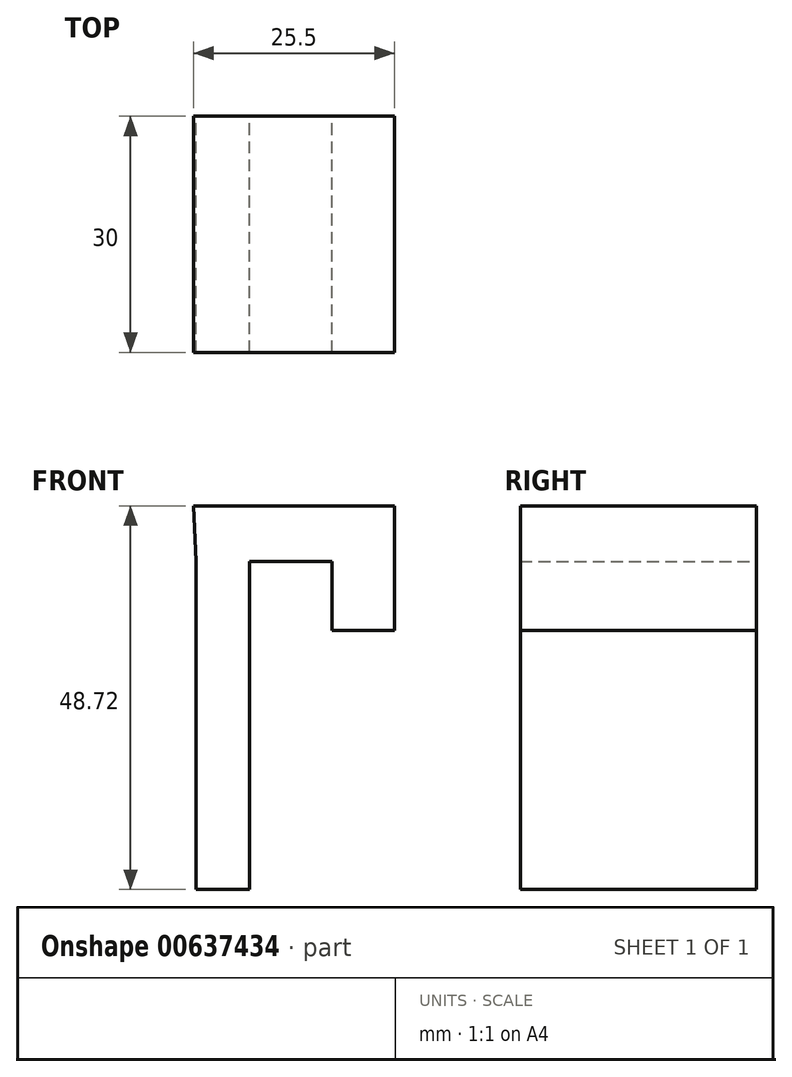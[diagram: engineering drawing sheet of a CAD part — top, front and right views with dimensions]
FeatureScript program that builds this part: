
annotation { "Feature Type Name" : "Feature", "Feature Type Description" : "" }
export const myFeature = defineFeature(function(context is Context, id is Id, definition is map)
    precondition{}
    {
        {
            var Q0;
            Q0=qCreatedBy(makeId("Front.planeOp"),FACE);
            var sketch = newSketch(context, id + "F0", { "sketchPlane" : qUnion([Q0])});
            skLineSegment(sketch, "E0", {"start": v(-48.01, 25.07) * mm, "end": v(-48.01, -16.57) * mm});
            skLineSegment(sketch, "E1", {"start": v(-48.01, -16.57) * mm, "end": v(-41.22, -16.57) * mm});
            skLineSegment(sketch, "E2", {"start": v(-41.22, -16.57) * mm, "end": v(-41.22, 25.07) * mm});
            skLineSegment(sketch, "E3", {"start": v(-41.22, 25.07) * mm, "end": v(-30.74, 25.07) * mm});
            skLineSegment(sketch, "E4", {"start": v(-30.74, 25.07) * mm, "end": v(-30.74, 16.29) * mm});
            skLineSegment(sketch, "E5", {"start": v(-30.74, 16.29) * mm, "end": v(-22.8, 16.29) * mm});
            skLineSegment(sketch, "E6", {"start": v(-22.8, 16.29) * mm, "end": v(-22.8, 32.15) * mm});
            skLineSegment(sketch, "E7", {"start": v(-22.8, 32.15) * mm, "end": v(-48.3, 32.15) * mm});
            skLineSegment(sketch, "E8", {"start": v(-48.3, 32.15) * mm, "end": v(-48.01, 25.07) * mm});
            skSolve(sketch);
        }
        {
            var Q0;
            Q0 = qSketchRegion(id + "F0", true);
            extrude(context, id + "F1", {"entities" : qUnion([Q0]), "depth" : 30 * mm, "offsetDistance" : 25 * mm});
        }
    });
